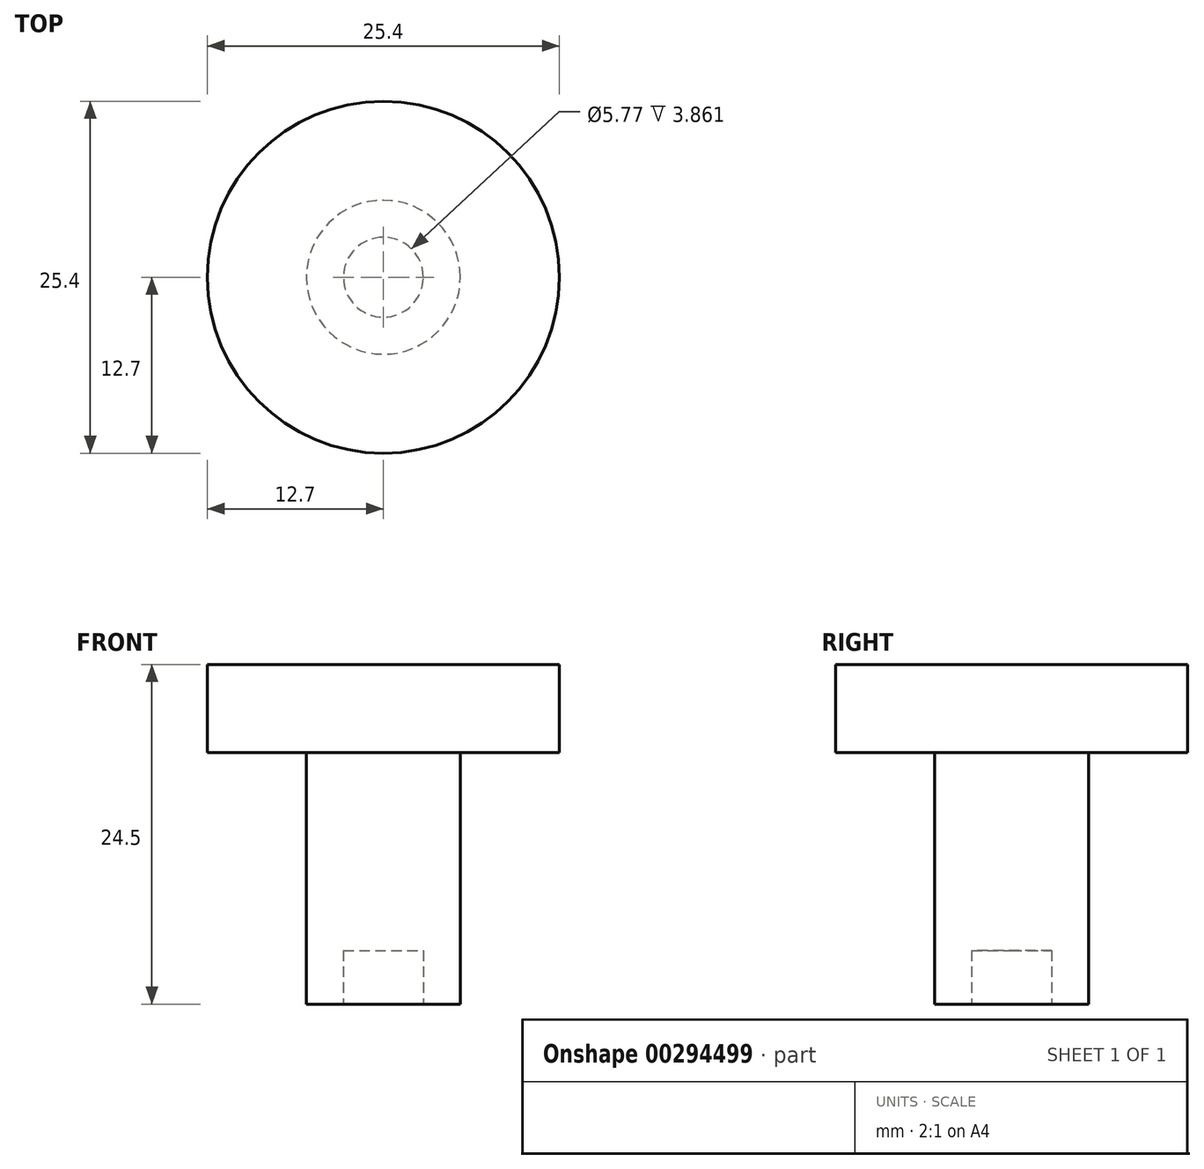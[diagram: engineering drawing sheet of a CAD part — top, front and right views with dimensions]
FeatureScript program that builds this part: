
annotation { "Feature Type Name" : "Feature", "Feature Type Description" : "" }
export const myFeature = defineFeature(function(context is Context, id is Id, definition is map)
    precondition{}
    {
        {
            var Q0;
            Q0=qCreatedBy(makeId("Top.planeOp"),FACE);
            var sketch = newSketch(context, id + "F0", { "sketchPlane" : qUnion([Q0])});
            skCircle(sketch, "E0", {"center": v(0, 0) * mm, "radius": 5.56 * mm});
            skSolve(sketch);
        }
        {
            var Q0;
            Q0=makeQuery(id+"F0.imprint","IMPRINT",FACE,{"disambiguationData":[TD([[makeQuery(id+"F0.imprint","IMPRINT",EDGE,{"derivedFrom":sQuery(id+"F0.wireOp",EDGE,"E0")}),1.0]])]});
            extrude(context, id + "F1", {"entities" : qUnion([Q0]), "depth" : 18.15 * mm});
        }
        {
            var Q0;
            Q0=makeQuery(id+"F1.opExtrude","CAP_FACE",FACE,{"disambiguationData":[OSD([sQuery(id+"F0.wireOp",EDGE,"E0")])],"isStart":false});
            var sketch = newSketch(context, id + "F2", { "sketchPlane" : qUnion([Q0])});
            skCircle(sketch, "E1", {"center": v(0, 0) * mm, "radius": 12.7 * mm});
            skSolve(sketch);
        }
        {
            var Q0;
            Q0 = qSketchRegion(id + "F2", true);
            extrude(context, id + "F3", {"entities" : qUnion([Q0]), "operationType" : NewBodyOperationType.ADD, "depth" : 6.35 * mm});
        }
        {
            var Q0;
            Q0=makeQuery(id+"F1.opExtrude","CAP_FACE",FACE,{"disambiguationData":[OSD([sQuery(id+"F0.wireOp",EDGE,"E0")])],"isStart":true});
            var sketch = newSketch(context, id + "F4", { "sketchPlane" : qUnion([Q0])});
            skCircle(sketch, "E2", {"center": v(0, 0) * mm, "radius": 2.88 * mm});
            skSolve(sketch);
        }
        {
            var Q0;
            Q0 = qSketchRegion(id + "F4", true);
            extrude(context, id + "F5", {"entities" : qUnion([Q0]), "operationType" : NewBodyOperationType.REMOVE, "oppositeDirection" : true, "depth" : 3.86 * mm});
        }
    });
